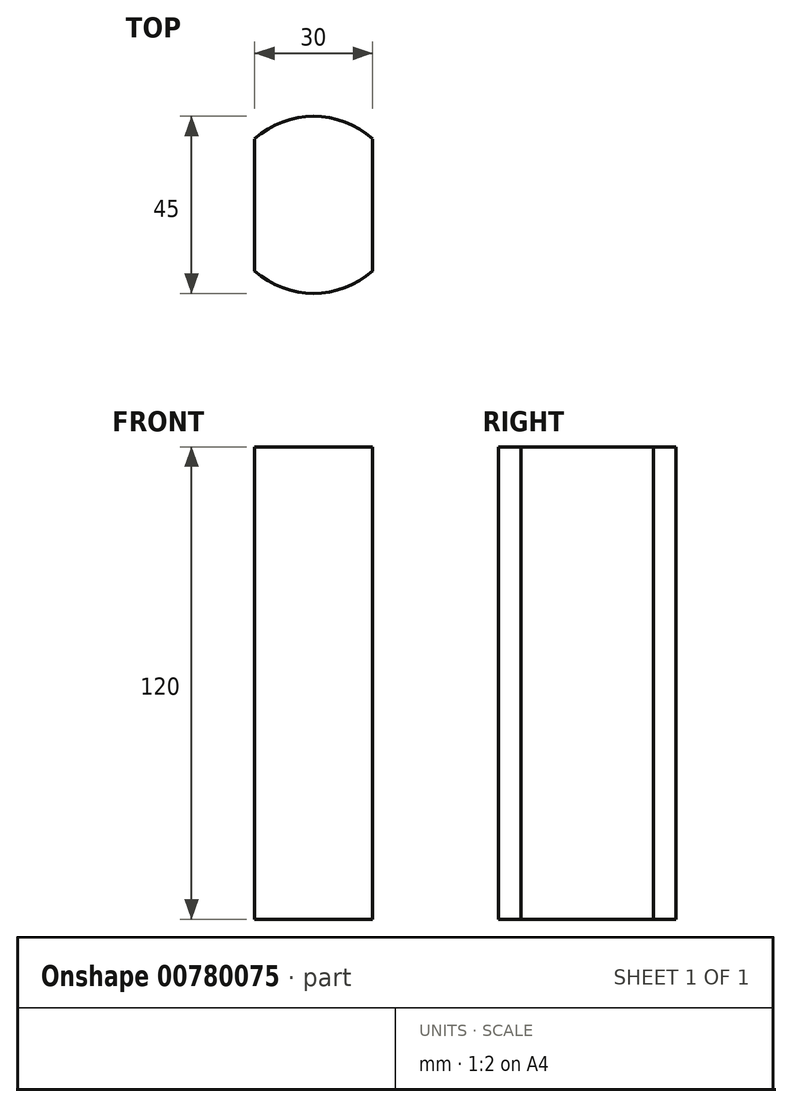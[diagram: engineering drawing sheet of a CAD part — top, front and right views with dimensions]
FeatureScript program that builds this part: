
annotation { "Feature Type Name" : "Feature", "Feature Type Description" : "" }
export const myFeature = defineFeature(function(context is Context, id is Id, definition is map)
    precondition{}
    {
        {
            var Q0;
            Q0=qCreatedBy(makeId("Top.planeOp"),FACE);
            var sketch = newSketch(context, id + "F0", { "sketchPlane" : qUnion([Q0])});
            skCircle(sketch, "E0", {"center": v(0, 0) * mm, "radius": 22.5 * mm});
            skLineSegment(sketch, "E1", {"start": v(-15, 16.77) * mm, "end": v(-15, -16.77) * mm});
            skLineSegment(sketch, "E2", {"start": v(15, 16.77) * mm, "end": v(15, -16.77) * mm});
            skSolve(sketch);
        }
        {
            var Q0;
            Q0=makeQuery(id+"F0.imprint","IMPRINT",FACE,{"disambiguationData":[TD([[makeQuery(id+"F0.imprint","IMPRINT",EDGE,{"derivedFrom":sQuery(id+"F0.wireOp",EDGE,"E0")}),1.0]])]});
            extrude(context, id + "F1", {"entities" : qUnion([Q0]), "depth" : 120 * mm, "offsetDistance" : 25 * mm});
        }
    });
